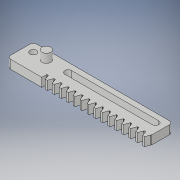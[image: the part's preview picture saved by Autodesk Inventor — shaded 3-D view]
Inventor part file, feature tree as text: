
AUTODESK INVENTOR PART (.ipt)
format: ipt  version: 2019 (Build 230136000, 136)  size: 248,832 bytes
history: native  units: in
note: dims shown in document units (in); Inventor stores cm internally (conversion verified against a paired STEP export)
features: sketch x4, extrude x3, hole x1, pattern_linear x1, fillet x1
ambient origin geometry x8: Origin, YZ Plane, XZ Plane, XY Plane, X Axis, Y Axis, Z Axis, Center Point
bodies: Solid1 (feature_tree)
feature tree (10):
  extrude  "Extrusion1"  Depth=0.5906in
  hole  "Hole2"  [1 undecoded]
  extrude  "Extrusion2"  Depth=0.1969in
  extrude  "Extrusion4"  Depth=0.0787in
  pattern_linear  "Rectangular Pattern1"  Spacing1=0.1969in  [1 undecoded]
  fillet  "Fillet1"  Radius=0.1969in
  sketch  "Sketch1"  dims[d0=3.1496in d1=0.5906in]
  sketch  "Sketch2"  dims[d6=0.1969in d7=0.0in d8=0.1969in]
  sketch  "Sketch3"  dims[d16=0.1969in]
  sketch  "Sketch5"  dims[d17=0.1495in d18=0.2362in d19=0.279in d20=0.0787in d21=0.5635in d22=0.315in d23=0.8108in d24=0.1969in d26=0.2953in d27=0.1969in d28=0.0in d47=0.1969in d48=0.0in d49=0.01in d50=0.01in d51=0.0194in d52=0.0421in d53=0.112in d54=0.1189in d55=0.01in d57=5.9055in d59=0.1571in d60=0.1969in d61=0.1495in d62=0.1495in d63=0.1969in d64=0.1969in d65=1.9685in d68=0.5906in d69=0.2362in d70=0.0787in]
note: 2 required parameter values undecoded (feature->parameter linkage not recoverable at this tier; creation-order binding heuristic only, values carry confidence <= 0.55)
